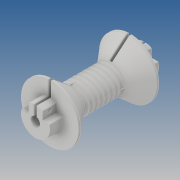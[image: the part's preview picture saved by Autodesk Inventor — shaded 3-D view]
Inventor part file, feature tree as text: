
AUTODESK INVENTOR PART (.ipt)
format: ipt  version: 2019 (Build 230136000, 136)  size: 309,248 bytes
history: native  units: mm
features: sketch x4, other x3, projected_geometry x3, extrude x2, hole x1, mirror x1, fillet x1
ambient origin geometry x8: Origin, YZ Plane, XZ Plane, XY Plane, X Axis, Y Axis, Z Axis, Center Point
bodies: Solide1 (feature_tree)
feature tree (15):
  other  "Révolution1"
  extrude  "Extrusion1"  Depth=6.3mm
  extrude  "Extrusion2"  Depth=20.0mm
  hole  "Perçage1"  [1 undecoded]
  mirror  "Symétrie1"
  other  "Hélicoïde1"
  fillet  "Congé1"  Radius=24.43461mm
  sketch  "Esquisse1"
  sketch  "Esquisse2"
  projected_geometry  "Boucle projetée1"
  sketch  "Esquisse3"
  projected_geometry  "Boucle projetée2"
  projected_geometry  "Boucle projetée3"
  sketch  "Esquisse5"
  other  "Projeter les arêtes coupées1"
note: 1 required parameter value undecoded (feature->parameter linkage not recoverable at this tier; creation-order binding heuristic only, values carry confidence <= 0.55)
